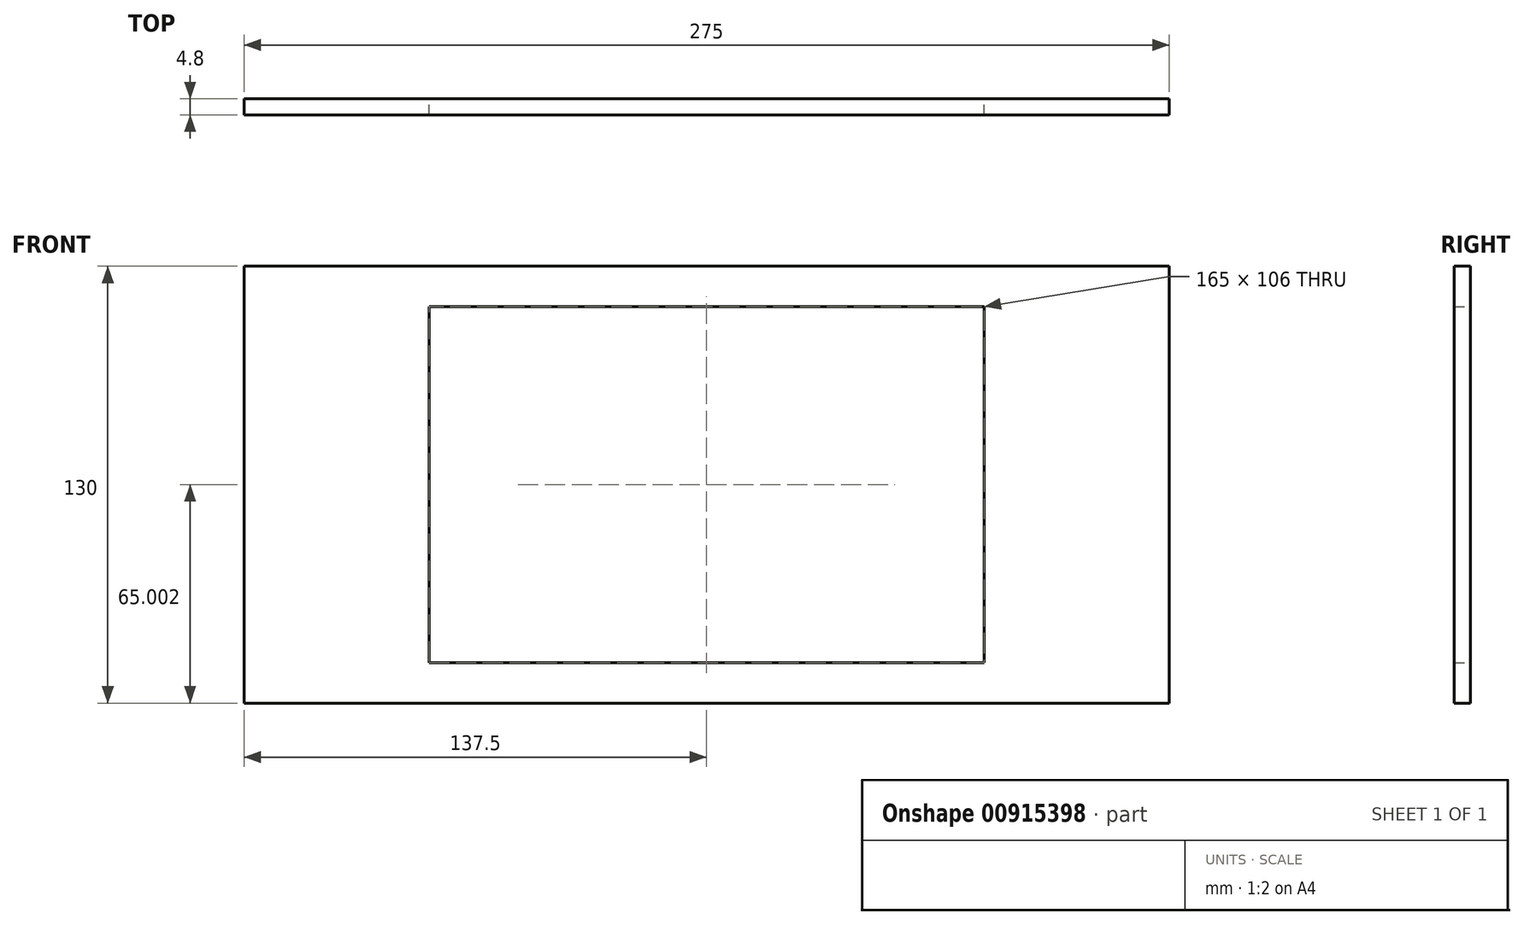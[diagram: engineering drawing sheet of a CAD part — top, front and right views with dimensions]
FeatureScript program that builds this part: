
annotation { "Feature Type Name" : "Feature", "Feature Type Description" : "" }
export const myFeature = defineFeature(function(context is Context, id is Id, definition is map)
    precondition{}
    {
        {
            var Q0;
            Q0=qCreatedBy(makeId("Front.planeOp"),FACE);
            var sketch = newSketch(context, id + "F0", { "sketchPlane" : qUnion([Q0])});
            skLineSegment(sketch, "E0.bottom", {"start": v(-174.16, 94.6) * mm, "end": v(100.84, 94.6) * mm});
            skLineSegment(sketch, "E0.top", {"start": v(-174.16, -35.4) * mm, "end": v(100.84, -35.4) * mm});
            skLineSegment(sketch, "E0.left", {"start": v(-174.16, 94.6) * mm, "end": v(-174.16, -35.4) * mm});
            skLineSegment(sketch, "E0.right", {"start": v(100.84, 94.6) * mm, "end": v(100.84, -35.4) * mm});
            skLineSegment(sketch, "E1.bottom", {"start": v(-119.16, 82.6) * mm, "end": v(45.84, 82.6) * mm});
            skLineSegment(sketch, "E1.top", {"start": v(-119.16, -23.4) * mm, "end": v(45.84, -23.4) * mm});
            skLineSegment(sketch, "E1.left", {"start": v(-119.16, 82.6) * mm, "end": v(-119.16, -23.4) * mm});
            skLineSegment(sketch, "E1.right", {"start": v(45.84, 82.6) * mm, "end": v(45.84, -23.4) * mm});
            skPoint(sketch, "E1.middle", {"position": v(-36.66, 29.6) * mm});
            skPoint(sketch, "E1.middle.positionSnap0", {"position": v(-36.66, 94.6) * mm});
            skPoint(sketch, "E1.centerSnap0", {"position": v(-36.66, 94.6) * mm});
            skPoint(sketch, "E2.orphan", {"position": v(-209.14, 34.6) * mm});
            skPoint(sketch, "E3.MirrorCS.start.orphan", {"position": v(-213.64, 34.6) * mm});
            skPoint(sketch, "E4.orphan", {"position": v(-215.03, 24.6) * mm});
            skPoint(sketch, "E5.MirrorCS.end.orphan", {"position": v(-210.23, 24.6) * mm});
            skPoint(sketch, "E6.MirrorCS.end.orphan", {"position": v(-174.16, 24.6) * mm});
            skPoint(sketch, "E7.MirrorCS.end.orphan", {"position": v(-213.64, 24.6) * mm});
            skPoint(sketch, "E8.orphan", {"position": v(-209.14, 29.6) * mm});
            skPoint(sketch, "E9.MirrorCS.end.orphan", {"position": v(-210.23, 29.6) * mm});
            skPoint(sketch, "E10.MirrorCS.end.orphan", {"position": v(-213.64, 29.6) * mm});
            skPoint(sketch, "E11.MirrorCS.start.orphan", {"position": v(-213.94, 34.6) * mm});
            skPoint(sketch, "E12.orphan", {"position": v(135.82, 34.6) * mm});
            skPoint(sketch, "E13.MirrorCS.start.orphan", {"position": v(136.91, 29.6) * mm});
            skPoint(sketch, "E14.orphan", {"position": v(135.82, 29.6) * mm});
            skPoint(sketch, "E15.start.orphan", {"position": v(140.32, 29.6) * mm});
            skPoint(sketch, "E16.orphan", {"position": v(141.71, 24.6) * mm});
            skPoint(sketch, "E17.end.orphan", {"position": v(100.84, 24.6) * mm});
            skPoint(sketch, "E18.MirrorCS.end.orphan", {"position": v(136.91, 24.6) * mm});
            skPoint(sketch, "E18.MirrorCS.start.orphan", {"position": v(140.32, 24.6) * mm});
            skPoint(sketch, "E19.MirrorCS.end.orphan", {"position": v(140.32, 34.6) * mm});
            skPoint(sketch, "E19.MirrorCS.start.orphan", {"position": v(140.62, 34.6) * mm});
            skPoint(sketch, "E20.trimOffspring.end.orphan", {"position": v(-36.66, -35.4) * mm});
            skSolve(sketch);
        }
        {
            var Q0;
            {var subQ3=sQuery(id+"F0.wireOp",EDGE,"E0.bottom");Q0=makeQuery(id+"F0.imprint","IMPRINT",FACE,{"disambiguationData":[TD([[makeQuery(id+"F0.imprint","IMPRINT",EDGE,{"derivedFrom":subQ3}),-1.0]])]});}
            var Q1;
            {var subQ0=sQuery(id+"F0.wireOp",EDGE,"e48a3bb5-675e-42eb-a290-356319898c6b3.MirrorCS");Q1=makeQuery(id+"F0.imprint","IMPRINT",FACE,{"disambiguationData":[TD([[makeQuery(id+"F0.imprint","IMPRINT",EDGE,{"derivedFrom":subQ0}),-1.0]])]});}
            var Q2;
            Q2=makeQuery(id+"F0.imprint","IMPRINT",FACE,{"disambiguationData":[TD([[makeQuery(id+"F0.imprint","IMPRINT",EDGE,{"derivedFrom":sQuery(id+"F0.wireOp",EDGE,"e48a3bb5-675e-42eb-a290-356319898c6b1.MirrorCS")}),1.0]])]});
            var Q3;
            {var subQ0=sQuery(id+"F0.wireOp",EDGE,"E13.MirrorCS");Q3=makeQuery(id+"F0.imprint","IMPRINT",FACE,{"disambiguationData":[TD([[makeQuery(id+"F0.imprint","IMPRINT",EDGE,{"derivedFrom":subQ0}),1.0]])]});}
            var Q4;
            {var subQ0=sQuery(id+"F0.wireOp",EDGE,"E13.MirrorCS");Q4=makeQuery(id+"F0.imprint","IMPRINT",FACE,{"disambiguationData":[TD([[makeQuery(id+"F0.imprint","IMPRINT",EDGE,{"derivedFrom":subQ0}),-1.0]])]});}
            var Q5;
            {var subQ5=sQuery(id+"F0.wireOp",EDGE,"E9.MirrorCS");var subQ7=makeQuery(id+"F0.imprint","IMPRINT",VERTEX,{"derivedFrom":subQ5});Q5=makeQuery(id+"F0.imprint","IMPRINT",FACE,{"disambiguationData":[TD([[makeQuery(id+"F0.imprint","IMPRINT",EDGE,{"disambiguationData":[TD([[subQ7,1.0]])],"derivedFrom":subQ5}),-1.0]])]});}
            var Q6;
            {var subQ6=sQuery(id+"F0.wireOp",EDGE,"W8B56JJR-NiTp-jr3x-Jou0-mrKQW3mr2Dtd");Q6=makeQuery(id+"F0.imprint","IMPRINT",FACE,{"disambiguationData":[TD([[makeQuery(id+"F0.imprint","IMPRINT",EDGE,{"derivedFrom":subQ6}),1.0]])]});}
            var Q7;
            {var subQ0=sQuery(id+"F0.wireOp",EDGE,"p7hgmXp2-HXYr-Fj9O-UAaj-zPTuF4fCcQ3S");var subQ3=makeQuery(id+"F0.imprint","IMPRINT",VERTEX,{"derivedFrom":subQ0});Q7=makeQuery(id+"F0.imprint","IMPRINT",FACE,{"disambiguationData":[TD([[makeQuery(id+"F0.imprint","IMPRINT",EDGE,{"disambiguationData":[TD([[subQ3,1.0]])],"derivedFrom":subQ0}),1.0]])]});}
            var Q8;
            {var subQ3=sQuery(id+"F0.wireOp",EDGE,"p7hgmXp2-HXYr-Fj9O-UAaj-zPTuF4fCcQ3S");var subQ5=makeQuery(id+"F0.imprint","IMPRINT",VERTEX,{"derivedFrom":subQ3});Q8=makeQuery(id+"F0.imprint","IMPRINT",FACE,{"disambiguationData":[TD([[makeQuery(id+"F0.imprint","IMPRINT",EDGE,{"disambiguationData":[TD([[subQ5,1.0]])],"derivedFrom":subQ3}),-1.0]])]});}
            var Q9;
            {var subQ6=sQuery(id+"F0.wireOp",EDGE,"8082285a-e2fa-4614-99ae-afb9585412bc5.MirrorCS");Q9=makeQuery(id+"F0.imprint","IMPRINT",FACE,{"disambiguationData":[TD([[makeQuery(id+"F0.imprint","IMPRINT",EDGE,{"derivedFrom":subQ6}),-1.0]])]});}
            var Q10;
            {var subQ1=sQuery(id+"F0.wireOp",EDGE,"E6.MirrorCS");Q10=makeQuery(id+"F0.imprint","IMPRINT",FACE,{"disambiguationData":[TD([[makeQuery(id+"F0.imprint","IMPRINT",EDGE,{"derivedFrom":subQ1}),1.0]])]});}
            extrude(context, id + "F1", {"entities" : qUnion([Q0, Q1, Q2, Q3, Q4, Q5, Q6, Q7, Q8, Q9, Q10]), "depth" : 4.8 * mm, "offsetDistance" : 25 * mm});
        }
    });
